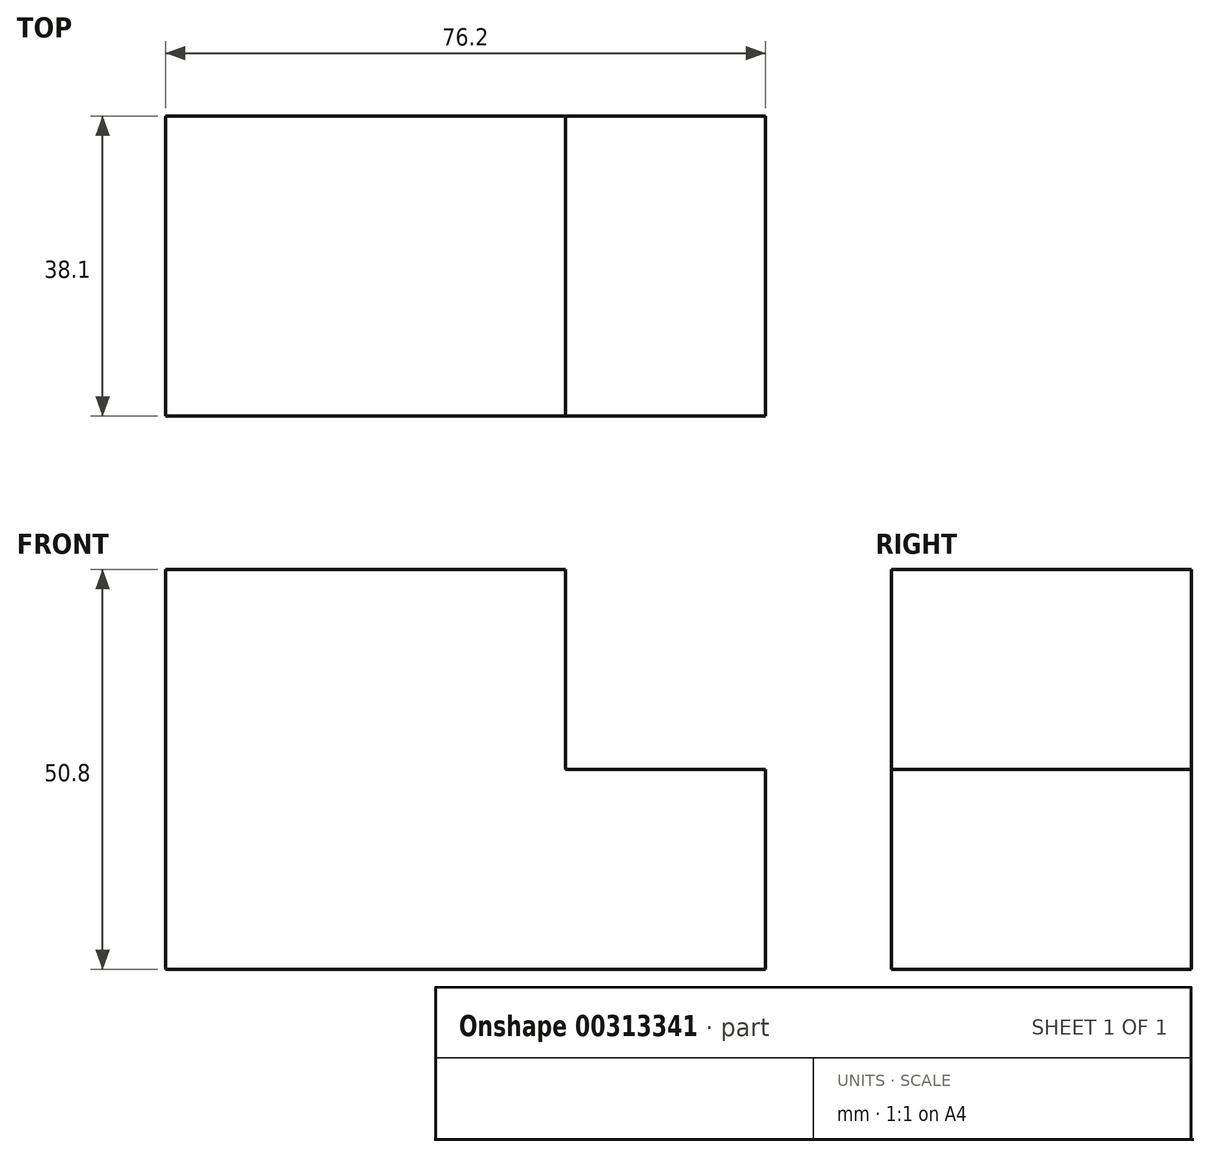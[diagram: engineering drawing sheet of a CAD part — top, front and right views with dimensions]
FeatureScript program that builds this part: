
annotation { "Feature Type Name" : "Feature", "Feature Type Description" : "" }
export const myFeature = defineFeature(function(context is Context, id is Id, definition is map)
    precondition{}
    {
        {
            var Q0;
            Q0=qCreatedBy(makeId("Front.planeOp"),FACE);
            var sketch = newSketch(context, id + "F0", { "sketchPlane" : qUnion([Q0])});
            skLineSegment(sketch, "E0", {"start": v(-36.67, -46.62) * mm, "end": v(39.53, -46.62) * mm});
            skLineSegment(sketch, "E1", {"start": v(-36.67, -46.62) * mm, "end": v(-36.67, 4.18) * mm});
            skLineSegment(sketch, "E2", {"start": v(-36.67, 4.18) * mm, "end": v(14.13, 4.18) * mm});
            skLineSegment(sketch, "E3", {"start": v(14.13, 4.18) * mm, "end": v(14.13, -21.22) * mm});
            skLineSegment(sketch, "E4", {"start": v(14.13, -21.22) * mm, "end": v(39.53, -21.22) * mm});
            skLineSegment(sketch, "E5", {"start": v(39.53, -21.22) * mm, "end": v(39.53, -46.62) * mm});
            skSolve(sketch);
        }
        {
            var Q0;
            Q0=makeQuery(id+"F0.imprint","IMPRINT",FACE,{"disambiguationData":[TD([[makeQuery(id+"F0.imprint","IMPRINT",EDGE,{"derivedFrom":sQuery(id+"F0.wireOp",EDGE,"E0")}),1.0]])]});
            extrude(context, id + "F1", {"entities" : qUnion([Q0]), "depth" : 38.1 * mm});
        }
    });
